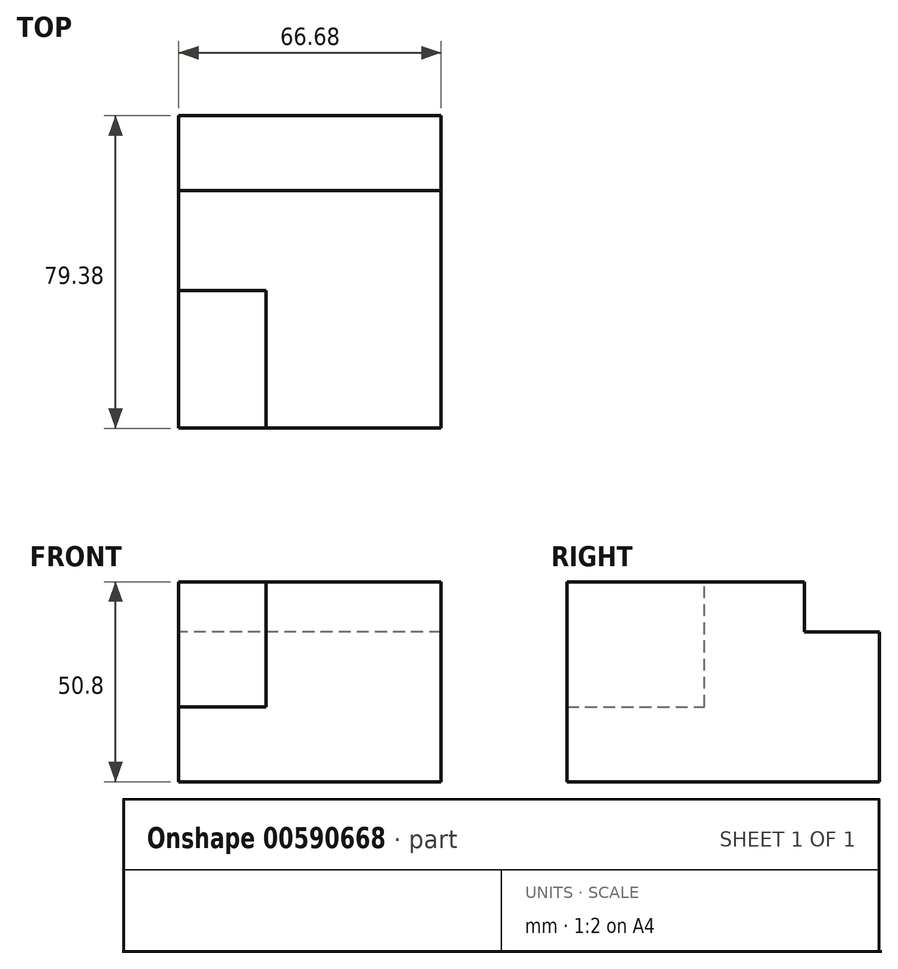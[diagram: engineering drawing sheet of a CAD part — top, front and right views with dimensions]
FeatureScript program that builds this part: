
annotation { "Feature Type Name" : "Feature", "Feature Type Description" : "" }
export const myFeature = defineFeature(function(context is Context, id is Id, definition is map)
    precondition{}
    {
        {
            var Q0;
            Q0=qCreatedBy(makeId("Top.planeOp"),FACE);
            var sketch = newSketch(context, id + "F0", { "sketchPlane" : qUnion([Q0])});
            skLineSegment(sketch, "E0.bottom", {"start": v(33.34, -39.69) * mm, "end": v(-33.34, -39.69) * mm});
            skLineSegment(sketch, "E0.top", {"start": v(33.34, 39.69) * mm, "end": v(-33.34, 39.69) * mm});
            skLineSegment(sketch, "E0.left", {"start": v(33.34, -39.69) * mm, "end": v(33.34, 39.69) * mm});
            skLineSegment(sketch, "E0.right", {"start": v(-33.34, -39.69) * mm, "end": v(-33.34, 39.69) * mm});
            skPoint(sketch, "E0.middle", {"position": v(0, 0) * mm});
            skSolve(sketch);
        }
        {
            var Q0;
            Q0 = qSketchRegion(id + "F0", true);
            extrude(context, id + "F1", {"entities" : qUnion([Q0]), "depth" : 50.8 * mm, "offsetDistance" : 25.4 * mm});
        }
        {
            var Q0;
            Q0=makeQuery(id+"F1.opExtrude","CAP_FACE",FACE,{"disambiguationData":[OSD([sQuery(id+"F0.wireOp",EDGE,"E0.bottom"),sQuery(id+"F0.wireOp",EDGE,"E0.top"),sQuery(id+"F0.wireOp",EDGE,"E0.left"),sQuery(id+"F0.wireOp",EDGE,"E0.right")])],"isStart":false});
            var sketch = newSketch(context, id + "F2", { "sketchPlane" : qUnion([Q0])});
            skLineSegment(sketch, "E1.bottom", {"start": v(-33.34, 39.69) * mm, "end": v(33.34, 39.69) * mm});
            skLineSegment(sketch, "E1.top", {"start": v(-33.34, 20.64) * mm, "end": v(33.34, 20.64) * mm});
            skLineSegment(sketch, "E1.left", {"start": v(-33.34, 39.69) * mm, "end": v(-33.34, 20.64) * mm});
            skLineSegment(sketch, "E1.right", {"start": v(33.34, 39.69) * mm, "end": v(33.34, 20.64) * mm});
            skSolve(sketch);
        }
        {
            var Q0;
            Q0 = qSketchRegion(id + "F2", true);
            extrude(context, id + "F3", {"entities" : qUnion([Q0]), "operationType" : NewBodyOperationType.REMOVE, "oppositeDirection" : true, "depth" : 12.7 * mm, "offsetDistance" : 25.4 * mm});
        }
        {
            var Q0;
            Q0=makeQuery(id+"F1.opExtrude","CAP_FACE",FACE,{"disambiguationData":[OSD([sQuery(id+"F0.wireOp",EDGE,"E0.bottom"),sQuery(id+"F0.wireOp",EDGE,"E0.top"),sQuery(id+"F0.wireOp",EDGE,"E0.left"),sQuery(id+"F0.wireOp",EDGE,"E0.right")])],"isStart":false});
            var sketch = newSketch(context, id + "F4", { "sketchPlane" : qUnion([Q0])});
            skLineSegment(sketch, "E2.bottom", {"start": v(-33.34, -39.69) * mm, "end": v(-11.11, -39.69) * mm});
            skLineSegment(sketch, "E2.top", {"start": v(-33.34, -4.76) * mm, "end": v(-11.11, -4.76) * mm});
            skLineSegment(sketch, "E2.left", {"start": v(-33.34, -39.69) * mm, "end": v(-33.34, -4.76) * mm});
            skLineSegment(sketch, "E2.right", {"start": v(-11.11, -39.69) * mm, "end": v(-11.11, -4.76) * mm});
            skSolve(sketch);
        }
        {
            var Q0;
            Q0 = qSketchRegion(id + "F4", true);
            extrude(context, id + "F5", {"entities" : qUnion([Q0]), "operationType" : NewBodyOperationType.REMOVE, "oppositeDirection" : true, "depth" : 31.75 * mm, "offsetDistance" : 25.4 * mm});
        }
    });
